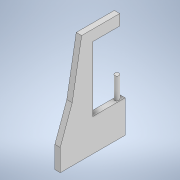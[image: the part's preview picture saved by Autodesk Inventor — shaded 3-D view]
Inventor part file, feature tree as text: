
AUTODESK INVENTOR PART (.ipt)
format: ipt  version: 2020.3 (Build 243373000, 373)  size: 120,320 bytes
history: native  units: mm
features: extrude x2, sketch x2, projected_geometry x1
ambient origin geometry x8: Origin, YZ Plane, XZ Plane, XY Plane, X Axis, Y Axis, Z Axis, Center Point
bodies: Solid1 (feature_tree)
feature tree (5):
  extrude  "Extrusion1"  Depth=30.0mm
  extrude  "Extrusion2"  Depth=60.0mm
  sketch  "Sketch1"  dims[d0=60.0mm d1=30.0mm]
  sketch  "Sketch2"  dims[d2=30.0mm d3=60.0mm d4=10.0mm d5=17.453293mm d7=25.0mm d8=27.925268mm d9=58.534001mm d10=10.0mm d11=35.0mm d12=35.0mm d13=5.0mm d14=0.0mm d15=4.0mm d16=25.0mm d17=20.0mm d18=0.0mm]
  projected_geometry  "Projected Loop1"
